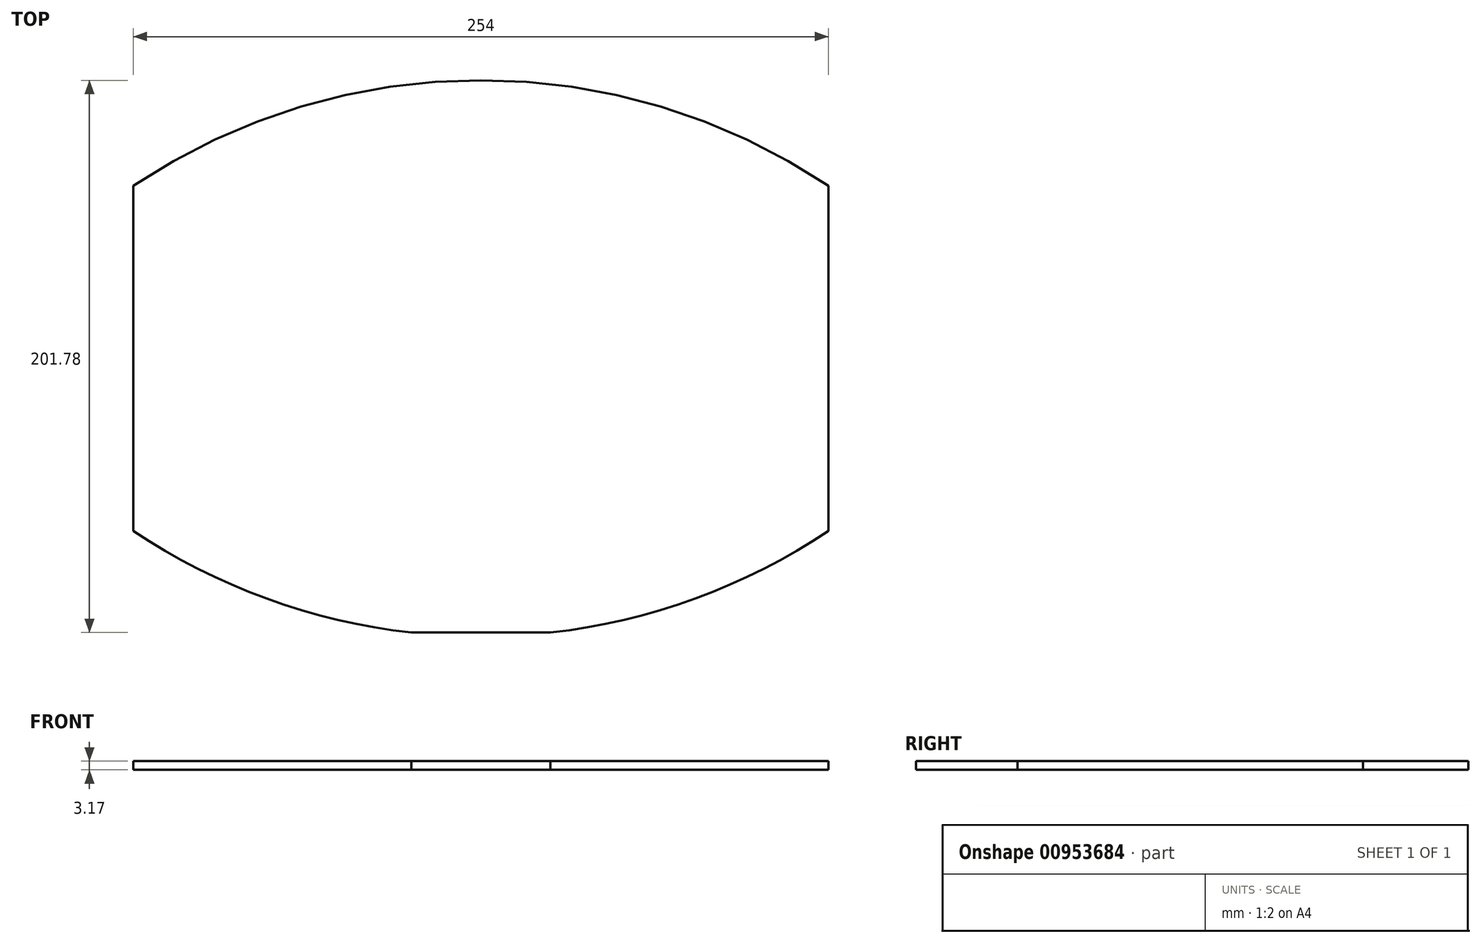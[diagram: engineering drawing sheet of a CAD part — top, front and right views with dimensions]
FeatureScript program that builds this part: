
annotation { "Feature Type Name" : "Feature", "Feature Type Description" : "" }
export const myFeature = defineFeature(function(context is Context, id is Id, definition is map)
    precondition{}
    {
        {
            var Q0;
            Q0=qCreatedBy(makeId("Top.planeOp"),FACE);
            var sketch = newSketch(context, id + "F0", { "sketchPlane" : qUnion([Q0])});
            skArc(sketch, "E0", {"start": v(127, 190.08) * mm, "mid": v(0, 228.6) * mm, "end": v(-127, 190.08) * mm});
            skArc(sketch, "E1", {"start": v(-127, 63.92) * mm, "mid": v(-78.43, 39.27) * mm, "end": v(-25.4, 26.82) * mm});
            skLineSegment(sketch, "E2.left", {"start": v(-127, 190.08) * mm, "end": v(-127, 63.92) * mm});
            skLineSegment(sketch, "E2.right", {"start": v(127, 190.08) * mm, "end": v(127, 63.92) * mm});
            skArc(sketch, "E3.trimOffspring", {"start": v(25.4, 26.82) * mm, "mid": v(78.43, 39.27) * mm, "end": v(127, 63.92) * mm});
            skLineSegment(sketch, "E4", {"start": v(-25.4, 26.82) * mm, "end": v(25.4, 26.82) * mm});
            skPoint(sketch, "E5.bottom.start.orphan", {"position": v(-25.4, 0) * mm});
            skSolve(sketch);
        }
        {
            var Q0;
            Q0=makeQuery(id+"F0.imprint","IMPRINT",FACE,{"disambiguationData":[TD([[makeQuery(id+"F0.imprint","IMPRINT",EDGE,{"derivedFrom":sQuery(id+"F0.wireOp",EDGE,"E0")}),1.0]])]});
            extrude(context, id + "F1", {"entities" : qUnion([Q0]), "depth" : 3.17 * mm, "offsetDistance" : 25.4 * mm});
        }
    });
